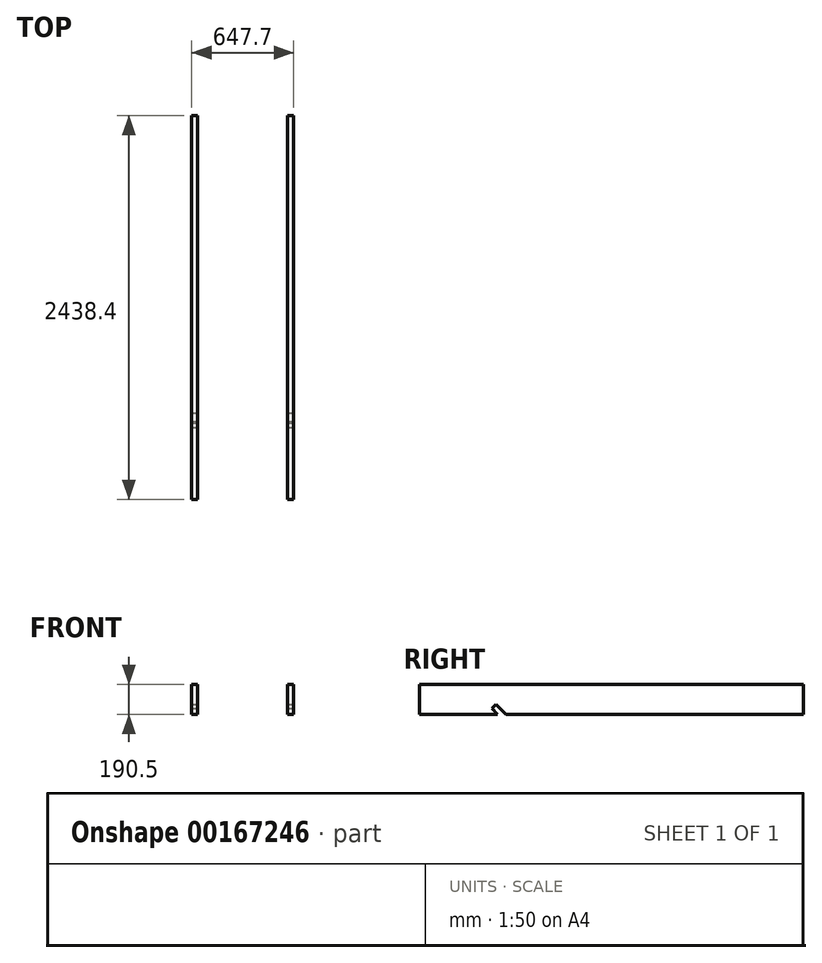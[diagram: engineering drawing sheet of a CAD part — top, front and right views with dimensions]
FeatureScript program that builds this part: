
annotation { "Feature Type Name" : "Feature", "Feature Type Description" : "" }
export const myFeature = defineFeature(function(context is Context, id is Id, definition is map)
    precondition{}
    {
        {
            var Q0;
            Q0=qCreatedBy(makeId("Front.planeOp"),FACE);
            var sketch = newSketch(context, id + "F0", { "sketchPlane" : qUnion([Q0])});
            skLineSegment(sketch, "E0.bottom", {"start": v(0, 0) * mm, "end": v(-38.1, 0) * mm});
            skLineSegment(sketch, "E0.top", {"start": v(0, 190.5) * mm, "end": v(-38.1, 190.5) * mm});
            skLineSegment(sketch, "E0.left", {"start": v(0, 0) * mm, "end": v(0, 190.5) * mm});
            skLineSegment(sketch, "E0.right", {"start": v(-38.1, 0) * mm, "end": v(-38.1, 190.5) * mm});
            skLineSegment(sketch, "E1.1.0.0", {"start": v(609.6, 190.5) * mm, "end": v(571.5, 190.5) * mm});
            skLineSegment(sketch, "E1.1.0.1", {"start": v(571.5, 0) * mm, "end": v(571.5, 190.5) * mm});
            skLineSegment(sketch, "E1.1.0.2", {"start": v(609.6, 0) * mm, "end": v(609.6, 190.5) * mm});
            skLineSegment(sketch, "E1.1.0.3", {"start": v(609.6, 0) * mm, "end": v(571.5, 0) * mm});
            skLineSegment(sketch, "E1.direction1", {"start": v(-38.1, 190.5) * mm, "end": v(571.5, 190.5) * mm, "construction": true});
            skSolve(sketch);
        }
        {
            var Q0;
            Q0=makeQuery(id+"F0.imprint","IMPRINT",FACE,{"disambiguationData":[TD([[makeQuery(id+"F0.imprint","IMPRINT",EDGE,{"derivedFrom":sQuery(id+"F0.wireOp",EDGE,"E0.bottom")}),-1.0]])]});
            var Q1;
            Q1=makeQuery(id+"F0.imprint","IMPRINT",FACE,{"disambiguationData":[TD([[makeQuery(id+"F0.imprint","IMPRINT",EDGE,{"derivedFrom":sQuery(id+"F0.wireOp",EDGE,"E1.1.0.0")}),1.0]])]});
            extrude(context, id + "F1", {"entities" : qUnion([Q0, Q1]), "depth" : 2438.4 * mm});
        }
        {
            var Q0;
            Q0=makeQuery(id+"F1.opExtrude","SWEPT_FACE",FACE,{"disambiguationData":[OSD([sQuery(id+"F0.wireOp",EDGE,"E1.1.0.2")])]});
            var sketch = newSketch(context, id + "F2", { "sketchPlane" : qUnion([Q0])});
            skLineSegment(sketch, "E2", {"start": v(-2438.4, 190.5) * mm, "end": v(-2133.6, 190.5) * mm, "construction": true});
            skLineSegment(sketch, "E3", {"start": v(-2133.6, 190.5) * mm, "end": v(-1943.1, 0) * mm, "construction": true});
            skLineSegment(sketch, "E4.0", {"start": v(-2079.72, 190.5) * mm, "end": v(-1889.22, 0) * mm, "construction": true});
            skLineSegment(sketch, "E5", {"start": v(-1943.1, 0) * mm, "end": v(-1980.13, 37.03) * mm});
            skLineSegment(sketch, "E6", {"start": v(-1980.13, 37.03) * mm, "end": v(-1953.2, 63.97) * mm});
            skLineSegment(sketch, "E7", {"start": v(-1953.2, 63.97) * mm, "end": v(-1889.22, 0) * mm});
            skLineSegment(sketch, "E8", {"start": v(-1889.22, 0) * mm, "end": v(-1943.1, 0) * mm});
            skSolve(sketch);
        }
        {
            var Q0;
            Q0=makeQuery(id+"F2.imprint","IMPRINT",FACE,{"disambiguationData":[TD([[makeQuery(id+"F2.imprint","IMPRINT",EDGE,{"derivedFrom":sQuery(id+"F2.wireOp",EDGE,"E5")}),-1.0]])]});
            extrude(context, id + "F3", {"entities" : qUnion([Q0]), "operationType" : NewBodyOperationType.REMOVE, "oppositeDirection" : true, "depth" : 914.4 * mm});
        }
    });
